# Revit family: WBW_F_2vak Hor_1vak Ver
name_source: partatom
category: Windows
revit_build: Autodesk Revit Architecture 2013 (Build: 20120221_2030(x64)
units: mm (PartAtom-declared; Revit-internal decimal feet)

## types (1)
- WBW_F_2vak Hor_1vak Ver
    Aanzicht Kader 110mm = No
    Aanzicht Kader 68mm = Yes
    Aanzicht Kader 78mm = No
    Aanzicht Kader 88mm = No
    Aanzicht Tussen Regel 110mm = No
    Aanzicht Tussen Regel 150mm = No
    Aanzicht Tussen Regel 200mm = Yes
    Aanzicht Tussen Regel 68mm = No
    Aanzicht Tussen Regel 78mm = No
    Aanzicht Tussen Regel 88mm = No
    Aanzicht Tussen Stijl 110mm = No
    Aanzicht Tussen Stijl 150mm = No
    Aanzicht Tussen Stijl 200mm = No
    Aanzicht Tussen Stijl 68mm = No
    Aanzicht Tussen Stijl 78mm = Yes
    Aanzicht Tussen Stijl 88mm = No
    AanzichtLijnDraai = No
    Aanzichtbreedte Kozijn Profielen_68_78_88_110_150mm = 68
    Aanzichtbreedte Tussen Regels _68_78_88_110_150_200mm = 200
    Aanzichtbreedte Tussen Stijlen _68_78_88_110_150_200mm = 78
    Analytic Construction = <None>
    Assembly Code = B2020110
    Beslag Resume 04 = Vaste beglazing
    Beslag Resume 05 = Niet inbraakwerend
    Brandwerend volgens: = -
    Brandwerendheid = No
    Brandwerendheid_old = No
    BreedteMaat_1 = 900 mm  [stored 2.95276 ft]
    BreedteMaat_2 = 1800 mm  [stored 5.90551 ft]
    BreedteMaat_3 = 0 mm  [stored 0 ft]
    BreedteMaat_4 = 0 mm  [stored 0 ft]
    BreedteMaat_5 = 0 mm  [stored 0 ft]
    Cost = 0 $
    Default Sill Height = 450 mm  [stored 1.47638 ft]
    Description = Kawneer RT 62 Raam volgens bijbehorende productomschrijving 'Standaard systeemomschrijving RT 62 standaard vlak'
    Diepte Versterking Binnenzijde_30_55_75 = 75 mm  [stored 0.246063 ft]
    Diepte Versterking Buitenzijde_30_50_85 = 30 mm  [stored 0.0984252 ft]
    Dikte Stelkozijn = 27 mm  [stored 0.0885827 ft]
    Dikte Stelkozijn onderzijde = 27 mm  [stored 0.0885827 ft]
    DikteStelkozijnOnderzijde_SpelingPui_BuitenbladMWOnderzijde = 17 mm  [stored 0.0557743 ft]
    DikteStelkozijn_SpelingPui_BuitenbladMW = 17 mm  [stored 0.0557743 ft]
    Glasdikte (totaal) = 29 mm  [stored 0.0951444 ft]
    GlassType = Glass, Clear Glazing, Low E
    HalveSpouw = 65 mm  [stored 0.213255 ft]
    HalveSpouw_OffsetVkKozijn_Stelkozijn = 78 mm  [stored 0.255906 ft]
    Height = 1800 mm  [stored 5.90551 ft]
    Hoogte Tussen regel 1 = 0 mm  [stored 0 ft]
    Hoogte Tussen regel 2 = 0 mm  [stored 0 ft]
    Hoogte Tussen regel 3 = 0 mm  [stored 0 ft]
    Hoogte Tussen regel 4 = 0 mm  [stored 0 ft]
    Hoogte Tussen regel 5 = 0 mm  [stored 0 ft]
    Keynote = 30.34
    Kleur Binnenzijde = Kawneer RAL 9010
    Kleur Binnenzijde Vleugel = Kawneer RAL 9010
    Kleur Buitenzijde = Kawneer RAL 9010
    Kleur Buitenzijde Vleugel = Kawneer RAL 9010
    Kleur H&S = NVT
    Model = NLSfb naam
    NL-SfB-Code = 31.21.22
    Nen 5096 R.c. 2 = No
    OffsetVkKozijnVkStelkozijn = 13 mm  [stored 0.0426509 ft]
    Operation = IfcWindow
    RT 52 = No
    RT 62 = Yes
    RT 72 = No
    ScheduleType |RF| = WBC_W_F
    Speling Pui_ buitenblad MW = 10 mm  [stored 0.0328084 ft]
    Speling Pui_buitenblad MW Onderzijde = 10 mm  [stored 0.0328084 ft]
    Spouwdiepte = 130 mm  [stored 0.426509 ft]
    Type Comments = Vrij te parameteriseren Revit Model
    URL = http://www.kawneer.com
    VerborgenVleugelVerzwaard = No
    Versterking Binnenzijde = Yes
    Versterking Buitenzijde = No
    Wall Closure = By host
    Width = 2700 mm  [stored 8.85827 ft]

note: [stored X ft] marks values corroborated as IEEE doubles in the binary element streams (Revit-internal decimal feet)

## geometry (parser evidence)
native form markers: Blend x22, Sweep x16
no freeform markers — native parametric forms only
